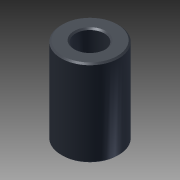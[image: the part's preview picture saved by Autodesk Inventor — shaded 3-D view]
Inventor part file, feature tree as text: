
AUTODESK INVENTOR PART (.ipt)
format: ipt  version: 2015 (Build 190159000, 159)  size: 87,040 bytes
history: native  units: mm
features: extrude x1, chamfer x1
ambient origin geometry x8: Origin, YZ Plane, XZ Plane, XY Plane, X Axis, Y Axis, Z Axis, Center Point
bodies: Solid1 (feature_tree)
feature tree (2):
  extrude  "Extrusión1"  Depth=4.0mm
  chamfer  "Chaflán1"  Distance=2.0mm
